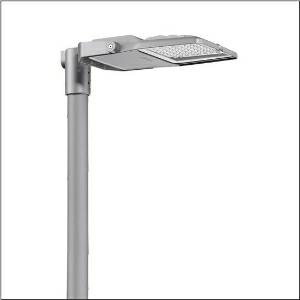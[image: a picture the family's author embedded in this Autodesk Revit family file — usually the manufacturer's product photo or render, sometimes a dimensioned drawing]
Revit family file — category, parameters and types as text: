
# Revit family: floodlight_fl_21_iq_mini___pl43_5xa7771c4a3a_be4f
name_source: partatom
category: Lighting Fixtures
units: mm (PartAtom-declared; Revit-internal decimal feet)

## family parameters
Cut with Voids When Loaded = No
Host = Face
Light Source = No
Part Type = Normal
Room Calculation Point = No
Round Connector Dimension = Use Diameter
Shared = No

## types (1)
- --- (1 x LED, 13050 lm, 87.2 W, 4000K)
    Apparent Load = 87 VA
    CIE Flux Codes = 27 78 99 100 100
    Color Rendering = 70
    Color Temperature = 4000K
    Default Elevation = 1800 mm
    Description = Floodlight FL 21 iQ mini, floodlight, primary light control with lens, of PMMA, primary optical cover: protective disc, of toughened safety glass, transparent, light distribution: PL43, light emission: direct distribution, installation type: surface-mounted, LED, High Power LED, rated luminous flux: 13.050lm, luminous efficacy: 150lm/W, light colour: 740, colour temperature: 4000K, control gear: iQ Comfort/DALI, control: Auto-Match, Temp-Guard, Lumen-Switch, Night-Set, Smart-Wire, Light-Fading, Desk-Remote (wireless, voltage-free reading and setting of iQ features in the workshop via application-optimized NFC function/RFID function), optimised constant luminous flux control (CLO 2.0), with terminal, 6-pole, mains connection: 220..240V, AC, 50/60Hz, start of lifetime: 87W, end of service life: 92W, reduction: 40W, luminaire housing, of diecast aluminium, powder-coated, Siteco® metallic grey (DB 702S), corrosivity category C5 mid according to DIN EN ISO 12944, suitable for swimming pools, chlorine-resistant, sealing non-destructively replaceable, please order mast flange separately, mast bracket, of steel, galvanised, powder-coated, Siteco® metallic grey (DB 702S), protection rating (complete): IP66, insulation class (complete): insulation class II (safety insulation), certification: CE, ENEC, VDE, protection symbol: D, impact resistance: IK08, permissible operating ambient temperature: -40..+40°C, permissible operating ambient temperature for outdoor applications: -40..+50°C, standard: DIN EN 12944, LABS conformity tested according to VDMA 24364:2018-05, packaging unit: 1 piece

Light Distribution: PL43
    Height = 70 mm
    Lamp = 1 x LED
    Lamp Light Flux = 13050 lm
    Lamp Power = 87.2 W
    Lamp count = 1
    Length = 485 mm
    Luminous efficacy = 150 lm/W
    Manufacturer = Siteco
    ModVariant = No
    Model = 5XA7771C4A3A
    Number of Poles = 1
    OnlyDefault = Yes
    Power Factor = 1
    Product Name = Floodlight FL 21 iQ mini | PL43
    Product group = floodlight | pylon annexe
    ProductGroupID = 6200
    Protection Class = Protection class II
    Protection Degree = IP 66
    RLX_Detail_Level = 1
    RLX_Emergency_Light_Flux = 0 lm
    RLX_Emergency_Type = 0
    RLX_Emergency_Type_DB = No
    RlxData = <blob elided: 101269 chars, md5=13d9784e>
    Socket = socket
    Standby Power = 0 W
    System Light Flux = 13050 lm
    System Power = 87 W
    Type Comments = factory setting: luminous flux: 100 % | dim-lin: 254 | 456 mA
    Type Image = l_1007125.jpg
    URL = http://relux.com
    VarID = @adj_162430
    Voltage = 0 V
    Weight = 0.00 kg
    Width = 337 mm

## geometry (parser evidence)
native form markers: Blend x4, Sweep x12
no freeform markers — native parametric forms only
